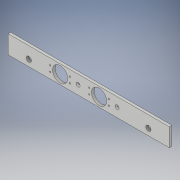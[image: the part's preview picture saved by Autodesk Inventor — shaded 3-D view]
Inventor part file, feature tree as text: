
AUTODESK INVENTOR PART (.ipt)
format: ipt  version: 2017 (Build 210142000, 142)  size: 138,752 bytes
history: native  units: in
note: dims shown in document units (in); Inventor stores cm internally (conversion verified against a paired STEP export)
features: extrude x2, sketch x1, chamfer x1
ambient origin geometry x8: Origin, YZ Plane, XZ Plane, XY Plane, X Axis, Y Axis, Z Axis, Center Point
bodies: Solid1 (feature_tree)
feature tree (4):
  sketch  "Sketch1"  dims[d3=1.46in d5=1.46in d10=0.14in d11=0.14in d24=0.276in d28=0.138in d29=0.138in d30=0.138in d31=0.945in d38=0.138in d39=0.138in d40=0.138in d41=0.138in d48=0.25in d49=0.0in d50=0.125in d51=0.125in d52=45.0deg d56=1.0in d57=0.0in d12=1.0in d13=1.0in]
  extrude  "Extrusion4"  Depth=0.125in
  chamfer  "Chamfer2"  Distance=0.14in
  extrude  "Extrusion5"  Depth=0.125in
